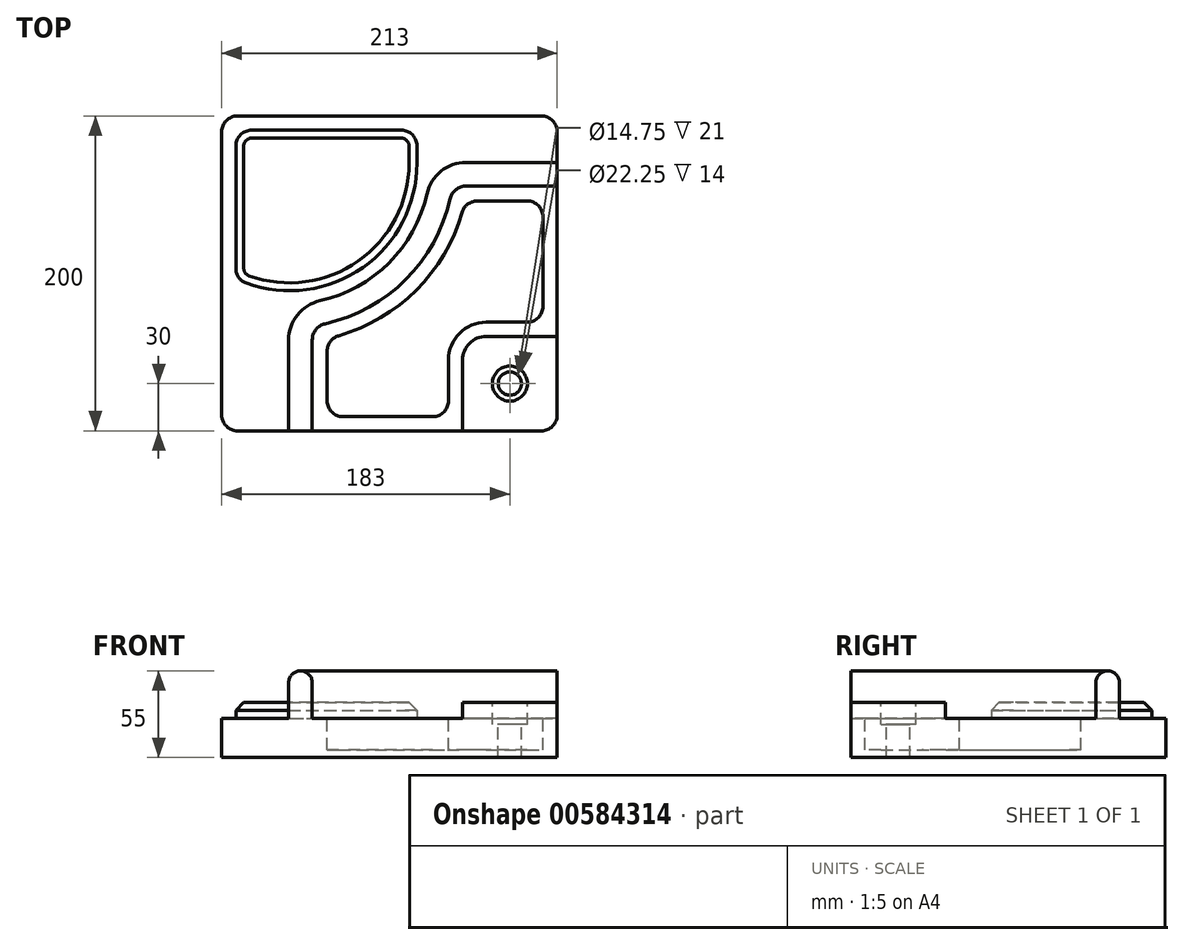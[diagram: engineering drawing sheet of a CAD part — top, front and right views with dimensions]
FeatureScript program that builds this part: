
annotation { "Feature Type Name" : "Feature", "Feature Type Description" : "" }
export const myFeature = defineFeature(function(context is Context, id is Id, definition is map)
    precondition{}
    {
        {
            var Q0;
            Q0=qCreatedBy(makeId("Top.planeOp"),FACE);
            var sketch = newSketch(context, id + "F0", { "sketchPlane" : qUnion([Q0])});
            skLineSegment(sketch, "E0.bottom", {"start": v(-96.5, 100) * mm, "end": v(96.5, 100) * mm});
            skLineSegment(sketch, "E0.top", {"start": v(-96.5, -100) * mm, "end": v(96.5, -100) * mm});
            skLineSegment(sketch, "E0.left", {"start": v(-106.5, 90) * mm, "end": v(-106.5, -90) * mm});
            skLineSegment(sketch, "E0.right", {"start": v(106.5, 90) * mm, "end": v(106.5, -90) * mm});
            skPoint(sketch, "E0.middle", {"position": v(0, 0) * mm});
            skPoint(sketch, "E1.visualSharp", {"position": v(-106.5, 100) * mm});
            skArc(sketch, "E1.filletArc", {"start": v(-96.5, 100) * mm, "mid": v(-103.57, 97.07) * mm, "end": v(-106.5, 90) * mm});
            skPoint(sketch, "E2.visualSharp", {"position": v(106.5, 100) * mm});
            skArc(sketch, "E2.filletArc", {"start": v(106.5, 90) * mm, "mid": v(103.57, 97.07) * mm, "end": v(96.5, 100) * mm});
            skPoint(sketch, "E3.visualSharp", {"position": v(106.5, -100) * mm});
            skArc(sketch, "E3.filletArc", {"start": v(96.5, -100) * mm, "mid": v(103.57, -97.07) * mm, "end": v(106.5, -90) * mm});
            skPoint(sketch, "E4.visualSharp", {"position": v(-106.5, -100) * mm});
            skArc(sketch, "E4.filletArc", {"start": v(-106.5, -90) * mm, "mid": v(-103.57, -97.07) * mm, "end": v(-96.5, -100) * mm});
            skLineSegment(sketch, "E5.bottom", {"start": v(96.5, -100) * mm, "end": v(-63.5, -100) * mm});
            skLineSegment(sketch, "E5.top", {"start": v(106.5, 70) * mm, "end": v(48.75, 70) * mm});
            skLineSegment(sketch, "E5.left", {"start": v(106.5, -90) * mm, "end": v(106.5, 70) * mm});
            skLineSegment(sketch, "E5.right", {"start": v(-63.5, -100) * mm, "end": v(-63.5, -42.25) * mm});
            skArc(sketch, "E6", {"start": v(-43.93, -17.85) * mm, "mid": v(0.14, 6.36) * mm, "end": v(24.35, 50.43) * mm});
            skPoint(sketch, "E7.visualSharp", {"position": v(-63.5, -20) * mm});
            skArc(sketch, "E7.filletArc", {"start": v(-43.93, -17.85) * mm, "mid": v(-58, -26.61) * mm, "end": v(-63.5, -42.25) * mm});
            skPoint(sketch, "E8.visualSharp", {"position": v(26.5, 70) * mm});
            skArc(sketch, "E8.filletArc", {"start": v(48.75, 70) * mm, "mid": v(33.11, 64.5) * mm, "end": v(24.35, 50.43) * mm});
            skLineSegment(sketch, "E9.0", {"start": v(-48.5, -100) * mm, "end": v(-48.5, -42.25) * mm});
            skLineSegment(sketch, "E9.1", {"start": v(106.5, 55) * mm, "end": v(48.75, 55) * mm});
            skArc(sketch, "E9.2", {"start": v(48.75, 55) * mm, "mid": v(42.5, 52.8) * mm, "end": v(38.99, 47.17) * mm});
            skArc(sketch, "E9.3", {"start": v(-40.67, -32.49) * mm, "mid": v(10.75, -4.25) * mm, "end": v(38.99, 47.17) * mm});
            skArc(sketch, "E9.4", {"start": v(-40.67, -32.49) * mm, "mid": v(-46.3, -36) * mm, "end": v(-48.5, -42.25) * mm});
            skLineSegment(sketch, "E10", {"start": v(46.5, -100) * mm, "end": v(46.5, -55) * mm});
            skLineSegment(sketch, "E11", {"start": v(61.5, -40) * mm, "end": v(106.5, -40) * mm});
            skPoint(sketch, "E12.centerSnap0", {"position": v(76.5, -40) * mm});
            skPoint(sketch, "E13", {"position": v(76.5, -70) * mm});
            skPoint(sketch, "E13.positionSnap0", {"position": v(46.5, -70) * mm});
            skPoint(sketch, "E14.visualSharp", {"position": v(46.5, -40) * mm});
            skArc(sketch, "E14.filletArc", {"start": v(61.5, -40) * mm, "mid": v(50.9, -44.4) * mm, "end": v(46.5, -55) * mm});
            skLineSegment(sketch, "E15.0", {"start": v(61.5, -31) * mm, "end": v(87.5, -31) * mm});
            skArc(sketch, "E15.1", {"start": v(61.5, -31) * mm, "mid": v(44.53, -38.03) * mm, "end": v(37.5, -55) * mm});
            skLineSegment(sketch, "E15.2", {"start": v(37.5, -81) * mm, "end": v(37.5, -55) * mm});
            skLineSegment(sketch, "E16.0", {"start": v(27.5, -91) * mm, "end": v(-29.5, -91) * mm});
            skArc(sketch, "E17.0", {"start": v(-32.24, -39.63) * mm, "mid": v(17.11, -10.61) * mm, "end": v(46.13, 38.74) * mm});
            skLineSegment(sketch, "E17.2", {"start": v(-39.5, -81) * mm, "end": v(-39.5, -49.25) * mm});
            skLineSegment(sketch, "E18.0", {"start": v(87.5, 46) * mm, "end": v(55.75, 46) * mm});
            skLineSegment(sketch, "E19.0", {"start": v(97.5, -21) * mm, "end": v(97.5, 36) * mm});
            skPoint(sketch, "E20.visualSharp", {"position": v(97.5, -31) * mm});
            skArc(sketch, "E20.filletArc", {"start": v(87.5, -31) * mm, "mid": v(94.57, -28.07) * mm, "end": v(97.5, -21) * mm});
            skPoint(sketch, "E21.visualSharp", {"position": v(97.5, 46) * mm});
            skArc(sketch, "E21.filletArc", {"start": v(97.5, 36) * mm, "mid": v(94.57, 43.07) * mm, "end": v(87.5, 46) * mm});
            skPoint(sketch, "E22.visualSharp", {"position": v(47.95, 46) * mm});
            skArc(sketch, "E22.filletArc", {"start": v(55.75, 46) * mm, "mid": v(49.72, 43.98) * mm, "end": v(46.13, 38.74) * mm});
            skPoint(sketch, "E23.visualSharp", {"position": v(-39.5, -91) * mm});
            skArc(sketch, "E23.filletArc", {"start": v(-39.5, -81) * mm, "mid": v(-36.57, -88.07) * mm, "end": v(-29.5, -91) * mm});
            skPoint(sketch, "E24.visualSharp", {"position": v(37.5, -91) * mm});
            skArc(sketch, "E24.filletArc", {"start": v(27.5, -91) * mm, "mid": v(34.57, -88.07) * mm, "end": v(37.5, -81) * mm});
            skPoint(sketch, "E25.visualSharp", {"position": v(-39.5, -41.45) * mm});
            skArc(sketch, "E25.filletArc", {"start": v(-32.24, -39.63) * mm, "mid": v(-37.48, -43.22) * mm, "end": v(-39.5, -49.25) * mm});
            skArc(sketch, "E26", {"start": v(-90.88, -6.23) * mm, "mid": v(-16.9, 3.75) * mm, "end": v(17.5, 70) * mm});
            skLineSegment(sketch, "E27.0", {"start": v(-87.5, 91) * mm, "end": v(7.5, 91) * mm});
            skLineSegment(sketch, "E28.0", {"start": v(-97.5, 81) * mm, "end": v(-97.5, 3.18) * mm});
            skLineSegment(sketch, "E29", {"start": v(17.5, 70) * mm, "end": v(17.5, 81) * mm});
            skPoint(sketch, "E30.visualSharp", {"position": v(17.5, 91) * mm});
            skArc(sketch, "E30.filletArc", {"start": v(17.5, 81) * mm, "mid": v(14.57, 88.07) * mm, "end": v(7.5, 91) * mm});
            skPoint(sketch, "E31.visualSharp", {"position": v(-97.5, 91) * mm});
            skArc(sketch, "E31.filletArc", {"start": v(-87.5, 91) * mm, "mid": v(-94.57, 88.07) * mm, "end": v(-97.5, 81) * mm});
            skPoint(sketch, "E32.visualSharp", {"position": v(-97.5, -3.52) * mm});
            skArc(sketch, "E32.filletArc", {"start": v(-97.5, 3.18) * mm, "mid": v(-95.68, -2.57) * mm, "end": v(-90.88, -6.23) * mm});
            skSolve(sketch);
        }
        {
            var Q0;
            Q0 = qSketchRegion(id + "F0", true);
            var Q1;
            Q1=makeQuery(id+"F0.imprint","IMPRINT",FACE,{"disambiguationData":[TD([[makeQuery(id+"F0.imprint","IMPRINT",EDGE,{"derivedFrom":sQuery(id+"F0.wireOp",EDGE,"E26")}),1.0]])]});
            var Q2;
            Q2=makeQuery(id+"F0.imprint","IMPRINT",FACE,{"disambiguationData":[TD([[makeQuery(id+"F0.imprint","IMPRINT",EDGE,{"derivedFrom":sQuery(id+"F0.wireOp",EDGE,"E15.0")}),1.0]])]});
            extrude(context, id + "F1", {"entities" : qUnion([Q0, Q1, Q2]), "oppositeDirection" : true, "depth" : 25 * mm, "offsetDistance" : 25 * mm});
        }
        {
            var Q0;
            {var subQ2=sQuery(id+"F0.wireOp",EDGE,"E3.filletArc");Q0=makeQuery(id+"F0.imprint","IMPRINT",FACE,{"disambiguationData":[TD([[makeQuery(id+"F0.imprint","IMPRINT",EDGE,{"derivedFrom":subQ2}),1.0]])]});}
            extrude(context, id + "F2", {"entities" : qUnion([Q0]), "operationType" : NewBodyOperationType.ADD, "depth" : 10 * mm, "offsetDistance" : 25 * mm});
        }
        {
            var Q0;
            Q0=makeQuery(id+"F0.imprint","IMPRINT",FACE,{"disambiguationData":[TD([[makeQuery(id+"F0.imprint","IMPRINT",EDGE,{"derivedFrom":sQuery(id+"F0.wireOp",EDGE,"E26")}),1.0]])]});
            extrude(context, id + "F3", {"entities" : qUnion([Q0]), "operationType" : NewBodyOperationType.ADD, "depth" : 10 * mm, "offsetDistance" : 25 * mm});
        }
        {
            var Q0;
            Q0=makeQuery(id+"F0.imprint","IMPRINT",FACE,{"disambiguationData":[TD([[makeQuery(id+"F0.imprint","IMPRINT",EDGE,{"derivedFrom":sQuery(id+"F0.wireOp",EDGE,"E15.0")}),1.0]])]});
            extrude(context, id + "F4", {"entities" : qUnion([Q0]), "operationType" : NewBodyOperationType.REMOVE, "oppositeDirection" : true, "depth" : 20 * mm, "offsetDistance" : 25 * mm});
        }
        {
            var Q0;
            Q0=makeQuery(id+"F2.opExtrude","CAP_FACE",FACE,{"disambiguationData":[OSD([sQuery(id+"F0.wireOp",EDGE,"E3.filletArc"),sQuery(id+"F0.wireOp",EDGE,"E5.bottom"),sQuery(id+"F0.wireOp",EDGE,"E5.left"),sQuery(id+"F0.wireOp",EDGE,"E10"),sQuery(id+"F0.wireOp",EDGE,"E11"),sQuery(id+"F0.wireOp",EDGE,"E14.filletArc")])],"isStart":false});
            var sketch = newSketch(context, id + "F5", { "sketchPlane" : qUnion([Q0])});
            skLineSegment(sketch, "E33.bottom", {"start": v(46.5, -100) * mm, "end": v(106.5, -100) * mm});
            skLineSegment(sketch, "E33.top", {"start": v(46.5, -40) * mm, "end": v(106.5, -40) * mm});
            skLineSegment(sketch, "E33.left", {"start": v(46.5, -100) * mm, "end": v(46.5, -40) * mm});
            skLineSegment(sketch, "E33.right", {"start": v(106.5, -100) * mm, "end": v(106.5, -40) * mm});
            skPoint(sketch, "E34", {"position": v(76.5, -70) * mm});
            skPoint(sketch, "E34.positionSnap0", {"position": v(46.5, -70) * mm});
            skPoint(sketch, "E34.positionSnap1", {"position": v(76.5, -40) * mm});
            skSolve(sketch);
        }
        {
            var Q0;
            Q0=sQuery(id+"F5.wireOp",VERTEX,"E34");
            var Q1;
            Q1=makeQuery(id+"F1.opExtrude","SWEPT_BODY",BODY,{"disambiguationData":[OSD([sQuery(id+"F0.wireOp",EDGE,"E0.bottom"),sQuery(id+"F0.wireOp",EDGE,"E0.top"),sQuery(id+"F0.wireOp",EDGE,"E0.left"),sQuery(id+"F0.wireOp",EDGE,"E0.right"),sQuery(id+"F0.wireOp",EDGE,"E1.filletArc"),sQuery(id+"F0.wireOp",EDGE,"E2.filletArc"),sQuery(id+"F0.wireOp",EDGE,"E3.filletArc"),sQuery(id+"F0.wireOp",EDGE,"E4.filletArc"),sQuery(id+"F0.wireOp",EDGE,"E5.bottom"),sQuery(id+"F0.wireOp",EDGE,"E5.left")])]});
            hole(context, id + "F6", {"style" : HoleStyle.C_BORE, "endStyle" : HoleEndStyle.THROUGH, "standardTappedOrClearance" : lookupTablePath({ "standard" : "ISO", "fit" : "Close", "size" : "M14", "type" : "Clearance" }), "standardBlindInLast" : lookupTablePath({ "fit" : "Close", "standard" : "ISO", "size" : "M14", "type" : "Clearance" }), "holeDiameter" : 14.75 * mm, "cBoreDiameter" : 22.25 * mm, "cBoreDepth" : 14 * mm, "majorDiameter" : 5 * mm, "isTappedThrough" : true, "tappedDepth" : 12 * mm, "tapClearance" : 3, "startFromSketch" : true, "locations" : qUnion([Q0]), "scope" : qUnion([Q1])});
        }
        {
            var Q0;
            {var subQ0=sQuery(id+"F0.wireOp",EDGE,"E5.bottom");Q0=makeQuery(id+"F2.boolean.opBoolean","MERGE",FACE,{"derivedFrom":[makeQuery(id+"F1.opExtrude","SWEPT_FACE",FACE,{"disambiguationData":[OSD([sQuery(id+"F0.wireOp",EDGE,"E0.top"),subQ0])]}),makeQuery(id+"F2.opExtrude","SWEPT_FACE",FACE,{"disambiguationData":[OSD([subQ0])]})]});}
            var sketch = newSketch(context, id + "F7", { "sketchPlane" : qUnion([Q0])});
            skLineSegment(sketch, "E35", {"start": v(0, 0) * mm, "end": v(-49, 0) * mm});
            skLineSegment(sketch, "E36", {"start": v(-49, 0) * mm, "end": v(-49, 22.5) * mm});
            skLineSegment(sketch, "E37", {"start": v(-64, 22.5) * mm, "end": v(-64, 0) * mm});
            skArc(sketch, "E38", {"start": v(-49, 22.5) * mm, "mid": v(-56.5, 30) * mm, "end": v(-64, 22.5) * mm});
            skLineSegment(sketch, "E39", {"start": v(-49, 0) * mm, "end": v(-64, 0) * mm});
            skSolve(sketch);
        }
        {
            var Q0;
            Q0=makeQuery(id+"F7.imprint","IMPRINT",FACE,{"disambiguationData":[TD([[makeQuery(id+"F7.imprint","IMPRINT",EDGE,{"derivedFrom":sQuery(id+"F7.wireOp",EDGE,"E36")}),1.0]])]});
            var Q1;
            Q1=sQuery(id+"F0.wireOp",EDGE,"E9.0");
            var Q2;
            Q2=sQuery(id+"F0.wireOp",EDGE,"E9.4");
            var Q3;
            Q3=sQuery(id+"F0.wireOp",EDGE,"E9.3");
            var Q4;
            Q4=sQuery(id+"F0.wireOp",EDGE,"E9.2");
            var Q5;
            Q5=sQuery(id+"F0.wireOp",EDGE,"E9.1");
            sweep(context, id + "F8", {"operationType" : NewBodyOperationType.ADD, "profiles" : qUnion([Q0]), "path" : qUnion([Q1, Q2, Q3, Q4, Q5])});
        }
        {
            var Q0;
            Q0=makeQuery(id+"F3.opExtrude","CAP_EDGE",EDGE,{"disambiguationData":[OSD([sQuery(id+"F0.wireOp",EDGE,"E28.0")])],"isStart":false});
            chamfer(context, id + "F9", {"entities" : qUnion([Q0]), "width" : 5 * mm, "tangentPropagation" : true});
        }
    });
